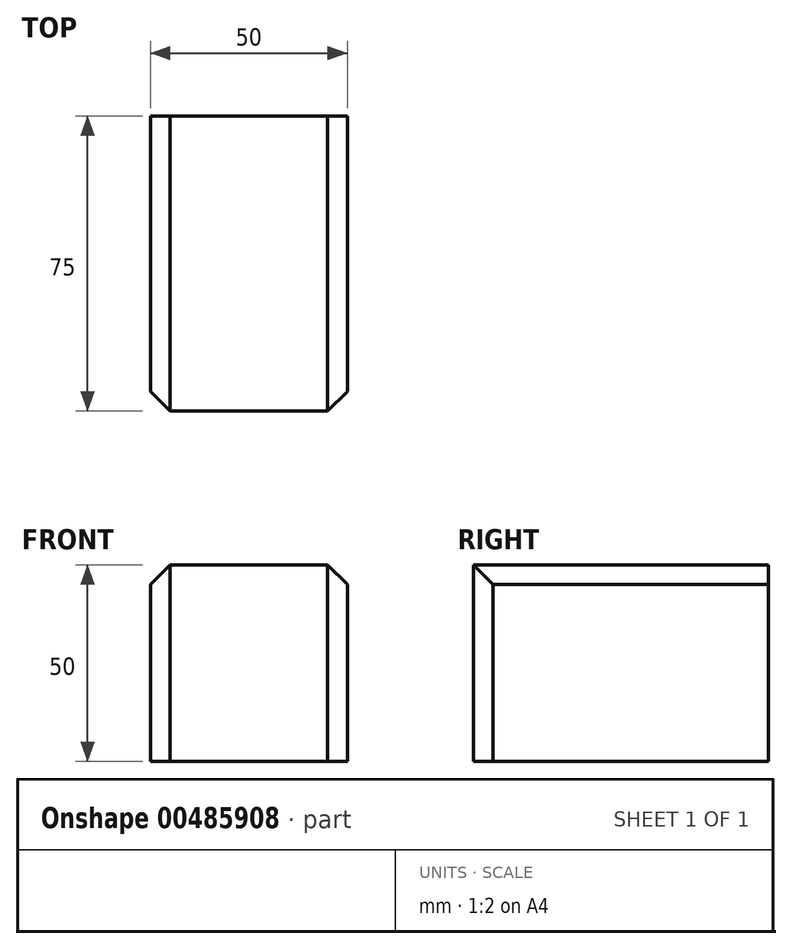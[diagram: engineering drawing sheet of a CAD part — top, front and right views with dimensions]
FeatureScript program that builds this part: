
annotation { "Feature Type Name" : "Feature", "Feature Type Description" : "" }
export const myFeature = defineFeature(function(context is Context, id is Id, definition is map)
    precondition{}
    {
        {
            var Q0;
            Q0=qCreatedBy(makeId("Front.planeOp"),FACE);
            var sketch = newSketch(context, id + "F0", { "sketchPlane" : qUnion([Q0])});
            skLineSegment(sketch, "E0", {"start": v(-50, 50) * mm, "end": v(0, 50) * mm});
            skLineSegment(sketch, "E1", {"start": v(0, 50) * mm, "end": v(0, 0) * mm});
            skLineSegment(sketch, "E2", {"start": v(0, 0) * mm, "end": v(-50, 0) * mm});
            skLineSegment(sketch, "E3", {"start": v(-50, 0) * mm, "end": v(-50, 50) * mm});
            skSolve(sketch);
        }
        {
            var Q0;
            Q0=makeQuery(id+"F0.imprint","IMPRINT",FACE,{"disambiguationData":[TD([[makeQuery(id+"F0.imprint","IMPRINT",EDGE,{"derivedFrom":sQuery(id+"F0.wireOp",EDGE,"E0")}),-1.0]])]});
            extrude(context, id + "F1", {"entities" : qUnion([Q0]), "depth" : 50 * mm, "hasSecondDirection" : true, "secondDirectionOppositeDirection" : true, "secondDirectionDepth" : 25 * mm});
        }
        {
            var Q0;
            Q0=makeQuery(id+"F1.opExtrude","SWEPT_EDGE",EDGE,{"disambiguationData":[OSD([sQuery(id+"F0.wireOp",EDGE,"E0"),sQuery(id+"F0.wireOp",EDGE,"E1")])]});
            var Q1;
            Q1=makeQuery(id+"F1.opExtrude","CAP_EDGE",EDGE,{"disambiguationData":[OSD([sQuery(id+"F0.wireOp",EDGE,"E1")])],"isStart":false});
            var Q2;
            Q2=makeQuery(id+"F1.opExtrude","CAP_EDGE",EDGE,{"disambiguationData":[OSD([sQuery(id+"F0.wireOp",EDGE,"E3")])],"isStart":false});
            var Q3;
            Q3=makeQuery(id+"F1.opExtrude","SWEPT_EDGE",EDGE,{"disambiguationData":[OSD([sQuery(id+"F0.wireOp",EDGE,"E0"),sQuery(id+"F0.wireOp",EDGE,"E3")])]});
            chamfer(context, id + "F2", {"entities" : qUnion([Q0, Q1, Q2, Q3]), "width" : 5 * mm, "tangentPropagation" : true});
        }
    });
